# Revit family: Hekatron_Feststellanlagen_AFS 65_DE_22.01
name_source: partatom
category: Brandmelder
revit_build: Autodesk Revit 2018 (Build: 20190510_1515(x64)
units: mm (PartAtom-declared; Revit-internal decimal feet)

## family parameters
Basisbauteil = Fläche
Beim Laden mit Abzugskörper schneiden = Nein
Bemaßung runder Anschluss = Durchmesser verwenden
Beschriftungsausrichtung beibehalten = Ja
Gemeinsam genutzt = Nein
OmniClass-Nummer = 23.85.30.21
OmniClass-Titel = Environmental Detection/Registration
Raumberechnungspunkt = Nein
Teiletyp = Normal

## types (1)
- AFS 65
    Beschreibung = Ankerplatte, Durchmesser 65mm, für extreme Einstellungen, passend zum THM 425.
    Breite (mm) = 75.0
    Farbe = silber/schwarz
    Hersteller = Hekatron
    Höhe (mm) = 55.0
    Link zu Ausschreibungstext = https://www.meinhplus.de
    Link zu Produktinformation = https://www.hekatron-planungstools.de
    Link zu ausschreiben.de = http://www.ausschreiben.de
    Material = Kunststoff
Metall
    Modell = AFS 65
    Montageart = Türmontage
    Tiefe (mm) = 75.0
    Typenkommentare = Flexible Winkelankerplatte AFS 65
    UB A&S Artikel Nummer = 6500178
    URL = https://www.hekatron-brandschutz.de
    Version des BIM Objektes = 22.01
    Vorgabe-Ansicht = 1200 mm

## geometry (parser evidence)
native form markers: Sweep x1
no freeform markers — native parametric forms only
